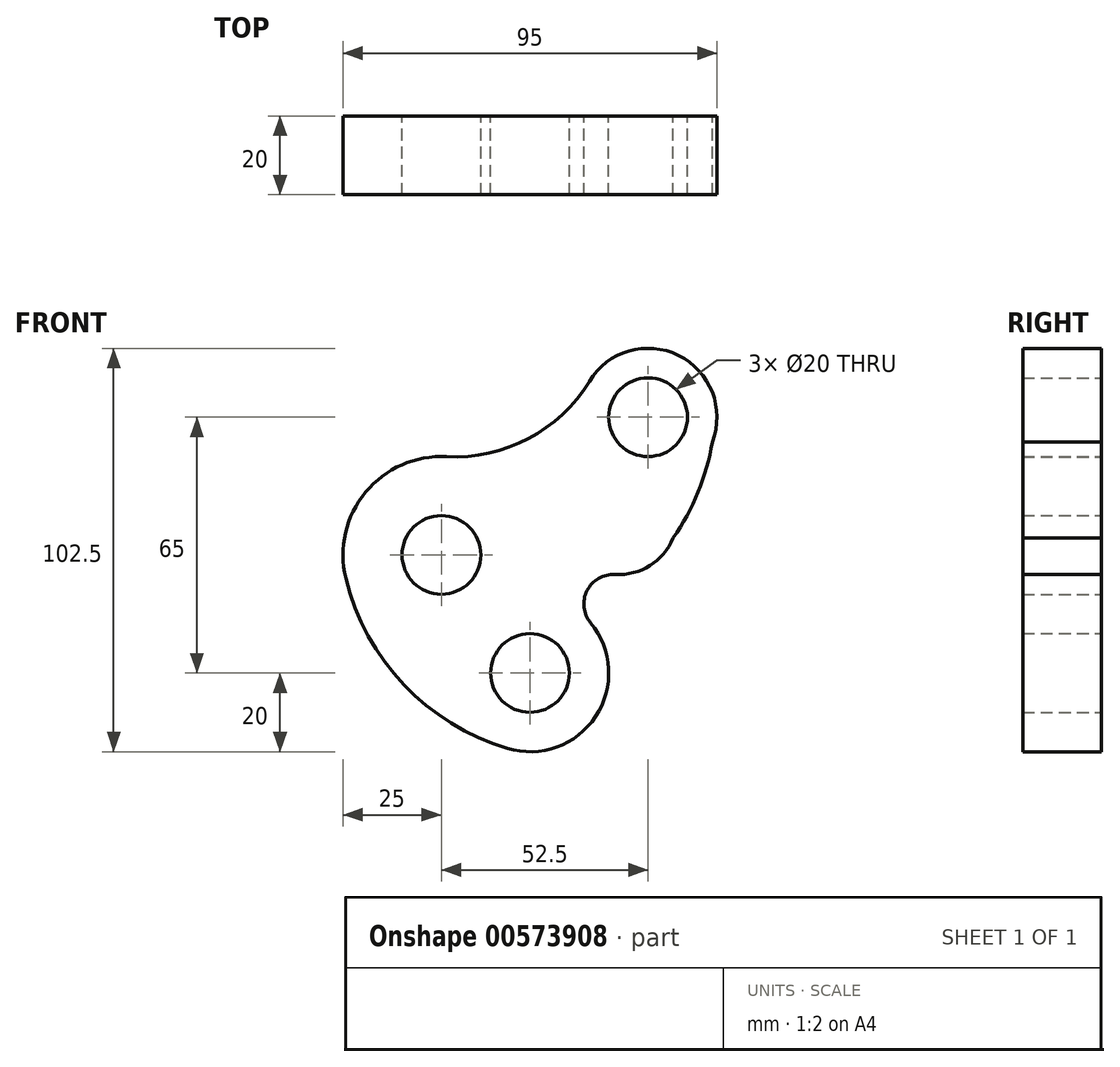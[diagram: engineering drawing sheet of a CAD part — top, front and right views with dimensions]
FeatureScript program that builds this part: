
annotation { "Feature Type Name" : "Feature", "Feature Type Description" : "" }
export const myFeature = defineFeature(function(context is Context, id is Id, definition is map)
    precondition{}
    {
        {
            var Q0;
            Q0=qCreatedBy(makeId("Front.planeOp"),FACE);
            var sketch = newSketch(context, id + "F0", { "sketchPlane" : qUnion([Q0])});
            skCircle(sketch, "E0", {"center": v(0, 0) * mm, "radius": 10 * mm});
            skCircle(sketch, "E1", {"center": v(22.5, -30) * mm, "radius": 10 * mm});
            skCircle(sketch, "E2", {"center": v(52.5, 35) * mm, "radius": 10 * mm});
            skArc(sketch, "E3", {"start": v(1.3, 24.97) * mm, "mid": v(-19.26, 15.94) * mm, "end": v(-24.28, -5.94) * mm});
            skArc(sketch, "E4", {"start": v(16.75, -49.16) * mm, "mid": v(39.17, -41.05) * mm, "end": v(37.9, -17.24) * mm});
            skArc(sketch, "E5", {"start": v(68.83, 28.7) * mm, "mid": v(60.23, 50.7) * mm, "end": v(37.55, 44.1) * mm});
            skArc(sketch, "E6", {"start": v(1.3, 24.97) * mm, "mid": v(22.07, 29.54) * mm, "end": v(37.55, 44.1) * mm});
            skArc(sketch, "E7", {"start": v(-24.28, -5.94) * mm, "mid": v(-9.51, -33) * mm, "end": v(16.75, -49.16) * mm});
            skArc(sketch, "E8", {"start": v(44.12, -4.97) * mm, "mid": v(52.97, -2.7) * mm, "end": v(58.86, 4.28) * mm});
            skArc(sketch, "E9", {"start": v(58.86, 4.28) * mm, "mid": v(65.2, 15.93) * mm, "end": v(68.83, 28.7) * mm});
            skArc(sketch, "E10", {"start": v(44.12, -4.97) * mm, "mid": v(37, -9.07) * mm, "end": v(37.9, -17.24) * mm});
            skSolve(sketch);
        }
        {
            var Q0;
            Q0 = qSketchRegion(id + "F0", true);
            extrude(context, id + "F1", {"entities" : qUnion([Q0]), "depth" : 20 * mm, "offsetDistance" : 25 * mm});
        }
    });
